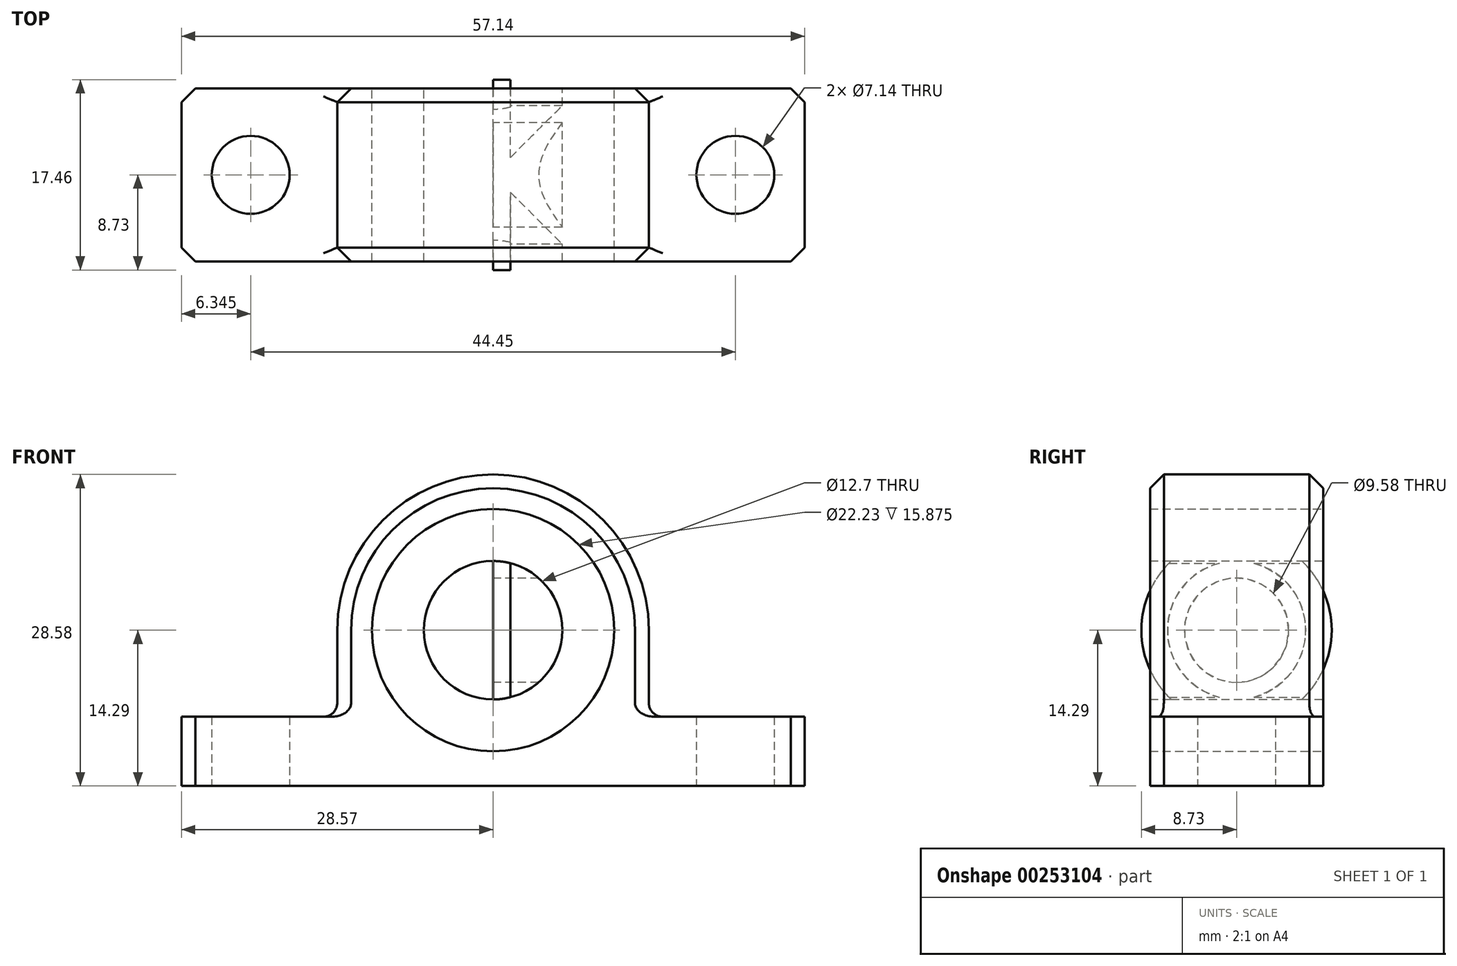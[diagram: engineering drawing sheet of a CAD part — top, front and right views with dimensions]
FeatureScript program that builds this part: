
annotation { "Feature Type Name" : "Feature", "Feature Type Description" : "" }
export const myFeature = defineFeature(function(context is Context, id is Id, definition is map)
    precondition{}
    {
        {
            var Q0;
            Q0=qCreatedBy(makeId("Front.planeOp"),FACE);
            var sketch = newSketch(context, id + "F0", { "sketchPlane" : qUnion([Q0])});
            skCircle(sketch, "E0", {"center": v(0, 0) * mm, "radius": 6.35 * mm});
            skCircle(sketch, "E1", {"center": v(0, 0) * mm, "radius": 14.29 * mm});
            skLineSegment(sketch, "E2", {"start": v(-28.58, -14.29) * mm, "end": v(28.58, -14.29) * mm});
            skLineSegment(sketch, "E3", {"start": v(0, -14.29) * mm, "end": v(0, 0) * mm, "construction": true});
            skLineSegment(sketch, "E4", {"start": v(-28.58, -14.29) * mm, "end": v(-28.58, -7.94) * mm});
            skLineSegment(sketch, "E5", {"start": v(-28.57, -7.94) * mm, "end": v(28.57, -7.94) * mm});
            skLineSegment(sketch, "E6", {"start": v(28.58, -7.94) * mm, "end": v(28.58, -14.29) * mm});
            skLineSegment(sketch, "E7", {"start": v(-14.29, -7.94) * mm, "end": v(-14.29, 0) * mm});
            skLineSegment(sketch, "E8", {"start": v(14.29, 0) * mm, "end": v(14.29, -7.94) * mm});
            skCircle(sketch, "E9", {"center": v(0, 0) * mm, "radius": 11.11 * mm});
            skSolve(sketch);
        }
        {
            var Q0;
            {var subQ1=sQuery(id+"F0.wireOp",EDGE,"E4");Q0=makeQuery(id+"F0.imprint","IMPRINT",FACE,{"disambiguationData":[TD([[makeQuery(id+"F0.imprint","IMPRINT",EDGE,{"derivedFrom":subQ1}),-1.0]])]});}
            var Q1;
            {var subQ0=sQuery(id+"F0.wireOp",EDGE,"E6");Q1=makeQuery(id+"F0.imprint","IMPRINT",FACE,{"disambiguationData":[TD([[makeQuery(id+"F0.imprint","IMPRINT",EDGE,{"derivedFrom":subQ0}),-1.0]])]});}
            var Q2;
            {var subQ1=sQuery(id+"F0.wireOp",EDGE,"E1");var subQ7=makeQuery(id+"F0.imprint","INTERSECT",VERTEX,{"derivedFrom":[subQ1,sQuery(id+"F0.wireOp",EDGE,"E2")]});Q2=makeQuery(id+"F0.imprint","IMPRINT",FACE,{"disambiguationData":[TD([[makeQuery(id+"F0.imprint","IMPRINT",EDGE,{"disambiguationData":[TD([[subQ7,1.0]])],"derivedFrom":subQ1}),1.0]])]});}
            var Q3;
            {var subQ1=sQuery(id+"F0.wireOp",EDGE,"E1");var subQ7=makeQuery(id+"F0.imprint","INTERSECT",VERTEX,{"derivedFrom":[subQ1,sQuery(id+"F0.wireOp",EDGE,"E7")]});Q3=makeQuery(id+"F0.imprint","IMPRINT",FACE,{"disambiguationData":[TD([[makeQuery(id+"F0.imprint","IMPRINT",EDGE,{"disambiguationData":[TD([[subQ7,1.0]])],"derivedFrom":subQ1}),1.0]])]});}
            var Q4;
            {var subQ0=sQuery(id+"F0.wireOp",EDGE,"E7");Q4=makeQuery(id+"F0.imprint","IMPRINT",FACE,{"disambiguationData":[TD([[makeQuery(id+"F0.imprint","IMPRINT",EDGE,{"derivedFrom":subQ0}),-1.0]])]});}
            var Q5;
            {var subQ0=sQuery(id+"F0.wireOp",EDGE,"E8");Q5=makeQuery(id+"F0.imprint","IMPRINT",FACE,{"disambiguationData":[TD([[makeQuery(id+"F0.imprint","IMPRINT",EDGE,{"derivedFrom":subQ0}),-1.0]])]});}
            extrude(context, id + "F1", {"entities" : qUnion([Q0, Q1, Q2, Q3, Q4, Q5]), "endBound" : BoundingType.SYMMETRIC, "depth" : 15.88 * mm});
        }
        {
            var Q0;
            Q0=makeQuery(id+"F0.imprint","IMPRINT",FACE,{"disambiguationData":[TD([[makeQuery(id+"F0.imprint","IMPRINT",EDGE,{"derivedFrom":sQuery(id+"F0.wireOp",EDGE,"E0")}),-1.0]])]});
            var Q1;
            {var subQ0=sQuery(id+"F0.wireOp",EDGE,"E9");var subQ1=sQuery(id+"F0.wireOp",EDGE,"E5");var subQ2=makeQuery(id+"F0.imprint","INTERSECT",VERTEX,{"disambiguationData":[OD(0.0)],"derivedFrom":[subQ1,subQ0]});Q1=makeQuery(id+"F0.imprint","IMPRINT",FACE,{"disambiguationData":[TD([[makeQuery(id+"F0.imprint","IMPRINT",EDGE,{"disambiguationData":[TD([[subQ2,-1.0]])],"derivedFrom":subQ1}),-1.0]])]});}
            extrude(context, id + "F2", {"entities" : qUnion([Q0, Q1]), "endBound" : BoundingType.SYMMETRIC, "depth" : 15.88 * mm});
        }
        {
            var Q0;
            Q0=makeQuery(id+"F1.opExtrude","CAP_EDGE",EDGE,{"disambiguationData":[OSD([sQuery(id+"F0.wireOp",EDGE,"E6")])],"isStart":true});
            var Q1;
            Q1=makeQuery(id+"F1.opExtrude","CAP_EDGE",EDGE,{"disambiguationData":[OSD([sQuery(id+"F0.wireOp",EDGE,"E4")])],"isStart":true});
            var Q2;
            Q2=makeQuery(id+"F1.opExtrude","CAP_EDGE",EDGE,{"disambiguationData":[OSD([sQuery(id+"F0.wireOp",EDGE,"E6")])],"isStart":false});
            var Q3;
            Q3=makeQuery(id+"F1.opExtrude","CAP_EDGE",EDGE,{"disambiguationData":[OSD([sQuery(id+"F0.wireOp",EDGE,"E4")])],"isStart":false});
            var Q4;
            Q4=makeQuery(id+"F1.opExtrude","CAP_EDGE",EDGE,{"disambiguationData":[OSD([sQuery(id+"F0.wireOp",EDGE,"E1")])],"isStart":false});
            var Q5;
            Q5=makeQuery(id+"F1.opExtrude","CAP_EDGE",EDGE,{"disambiguationData":[OSD([sQuery(id+"F0.wireOp",EDGE,"E1")])],"isStart":true});
            chamfer(context, id + "F3", {"entities" : qUnion([Q0, Q1, Q2, Q3, Q4, Q5]), "width" : 1.27 * mm, "tangentPropagation" : true});
        }
        {
            var Q0;
            Q0=makeQuery(id+"F1.opExtrude","SWEPT_EDGE",EDGE,{"disambiguationData":[OSD([sQuery(id+"F0.wireOp",EDGE,"E5"),sQuery(id+"F0.wireOp",EDGE,"E7")])]});
            var Q1;
            Q1=makeQuery(id+"F1.opExtrude","SWEPT_EDGE",EDGE,{"disambiguationData":[OSD([sQuery(id+"F0.wireOp",EDGE,"E5"),sQuery(id+"F0.wireOp",EDGE,"E8")])]});
            var Q2;
            {var subQ0=sQuery(id+"F0.wireOp",EDGE,"E5");var subQ1=sQuery(id+"F0.wireOp",EDGE,"E8");Q2=makeQuery(id+"F3.opChamfer","BLEND_EDGE",EDGE,{"blendedFrom":[makeQuery(id+"F1.opExtrude","CAP_EDGE",EDGE,{"disambiguationData":[OSD([subQ1])],"isStart":false}),makeQuery(id+"F1.opExtrude","SWEPT_FACE",FACE,{"disambiguationData":[OSD([subQ0]),TDD([makeQuery(id+"F0.imprint","IMPRINT",EDGE,{"disambiguationData":[TD([[makeQuery(id+"F0.imprint","INTERSECT",VERTEX,{"derivedFrom":[subQ0,sQuery(id+"F0.wireOp",EDGE,"E6")]}),1.0]])],"derivedFrom":subQ0})])]})],"blendedInto":[makeQuery(id+"F1.opExtrude","SWEPT_FACE",FACE,{"disambiguationData":[OSD([subQ0]),TDD([makeQuery(id+"F0.imprint","IMPRINT",EDGE,{"disambiguationData":[TD([[makeQuery(id+"F0.imprint","INTERSECT",VERTEX,{"derivedFrom":[subQ0,sQuery(id+"F0.wireOp",EDGE,"E6")]}),1.0]])],"derivedFrom":subQ0})])]})]});}
            var Q3;
            {var subQ0=sQuery(id+"F0.wireOp",EDGE,"E5");var subQ1=sQuery(id+"F0.wireOp",EDGE,"E8");Q3=makeQuery(id+"F3.opChamfer","BLEND_EDGE",EDGE,{"blendedFrom":[makeQuery(id+"F1.opExtrude","CAP_EDGE",EDGE,{"disambiguationData":[OSD([subQ1])],"isStart":true}),makeQuery(id+"F1.opExtrude","SWEPT_FACE",FACE,{"disambiguationData":[OSD([subQ0]),TDD([makeQuery(id+"F0.imprint","IMPRINT",EDGE,{"disambiguationData":[TD([[makeQuery(id+"F0.imprint","INTERSECT",VERTEX,{"derivedFrom":[subQ0,sQuery(id+"F0.wireOp",EDGE,"E6")]}),1.0]])],"derivedFrom":subQ0})])]})],"blendedInto":[makeQuery(id+"F1.opExtrude","SWEPT_FACE",FACE,{"disambiguationData":[OSD([subQ0]),TDD([makeQuery(id+"F0.imprint","IMPRINT",EDGE,{"disambiguationData":[TD([[makeQuery(id+"F0.imprint","INTERSECT",VERTEX,{"derivedFrom":[subQ0,sQuery(id+"F0.wireOp",EDGE,"E6")]}),1.0]])],"derivedFrom":subQ0})])]})]});}
            var Q4;
            {var subQ0=sQuery(id+"F0.wireOp",EDGE,"E5");var subQ1=sQuery(id+"F0.wireOp",EDGE,"E7");Q4=makeQuery(id+"F3.opChamfer","BLEND_EDGE",EDGE,{"blendedFrom":[makeQuery(id+"F1.opExtrude","CAP_EDGE",EDGE,{"disambiguationData":[OSD([subQ1])],"isStart":false}),makeQuery(id+"F1.opExtrude","SWEPT_FACE",FACE,{"disambiguationData":[OSD([subQ0]),TDD([makeQuery(id+"F0.imprint","IMPRINT",EDGE,{"disambiguationData":[TD([[makeQuery(id+"F0.imprint","INTERSECT",VERTEX,{"derivedFrom":[sQuery(id+"F0.wireOp",EDGE,"E4"),subQ0]}),-1.0]])],"derivedFrom":subQ0})])]})],"blendedInto":[makeQuery(id+"F1.opExtrude","SWEPT_FACE",FACE,{"disambiguationData":[OSD([subQ0]),TDD([makeQuery(id+"F0.imprint","IMPRINT",EDGE,{"disambiguationData":[TD([[makeQuery(id+"F0.imprint","INTERSECT",VERTEX,{"derivedFrom":[sQuery(id+"F0.wireOp",EDGE,"E4"),subQ0]}),-1.0]])],"derivedFrom":subQ0})])]})]});}
            var Q5;
            {var subQ0=sQuery(id+"F0.wireOp",EDGE,"E5");var subQ1=sQuery(id+"F0.wireOp",EDGE,"E7");Q5=makeQuery(id+"F3.opChamfer","BLEND_EDGE",EDGE,{"blendedFrom":[makeQuery(id+"F1.opExtrude","CAP_EDGE",EDGE,{"disambiguationData":[OSD([subQ1])],"isStart":true}),makeQuery(id+"F1.opExtrude","SWEPT_FACE",FACE,{"disambiguationData":[OSD([subQ0]),TDD([makeQuery(id+"F0.imprint","IMPRINT",EDGE,{"disambiguationData":[TD([[makeQuery(id+"F0.imprint","INTERSECT",VERTEX,{"derivedFrom":[sQuery(id+"F0.wireOp",EDGE,"E4"),subQ0]}),-1.0]])],"derivedFrom":subQ0})])]})],"blendedInto":[makeQuery(id+"F1.opExtrude","SWEPT_FACE",FACE,{"disambiguationData":[OSD([subQ0]),TDD([makeQuery(id+"F0.imprint","IMPRINT",EDGE,{"disambiguationData":[TD([[makeQuery(id+"F0.imprint","INTERSECT",VERTEX,{"derivedFrom":[sQuery(id+"F0.wireOp",EDGE,"E4"),subQ0]}),-1.0]])],"derivedFrom":subQ0})])]})]});}
            fillet(context, id + "F4", {"entities" : qUnion([Q0, Q1, Q2, Q3, Q4, Q5]), "radius" : 1.27 * mm, "allowEdgeOverflow" : false});
        }
        {
            var Q0;
            Q0=makeQuery(id+"F1.opExtrude","SWEPT_FACE",FACE,{"disambiguationData":[OSD([sQuery(id+"F0.wireOp",EDGE,"E2")])]});
            var sketch = newSketch(context, id + "F5", { "sketchPlane" : qUnion([Q0])});
            skCircle(sketch, "E10", {"center": v(-22.23, 0) * mm, "radius": 3.57 * mm});
            skPoint(sketch, "E10.centerSnap0", {"position": v(-28.58, 0) * mm});
            skLineSegment(sketch, "E11", {"start": v(0, 7.94) * mm, "end": v(0, -7.94) * mm, "construction": true});
            skCircle(sketch, "E12", {"center": v(22.23, 0) * mm, "radius": 3.57 * mm});
            skPoint(sketch, "E12.centerSnap0", {"position": v(28.58, 0) * mm});
            skSolve(sketch);
        }
        {
            var Q0;
            Q0=makeQuery(id+"F5.imprint","IMPRINT",FACE,{"disambiguationData":[TD([[makeQuery(id+"F5.imprint","IMPRINT",EDGE,{"derivedFrom":sQuery(id+"F5.wireOp",EDGE,"E10")}),1.0]])]});
            var Q1;
            Q1=makeQuery(id+"F5.imprint","IMPRINT",FACE,{"disambiguationData":[TD([[makeQuery(id+"F5.imprint","IMPRINT",EDGE,{"derivedFrom":sQuery(id+"F5.wireOp",EDGE,"E12")}),1.0]])]});
            extrude(context, id + "F6", {"entities" : qUnion([Q0, Q1]), "operationType" : NewBodyOperationType.REMOVE, "endBound" : BoundingType.THROUGH_ALL, "oppositeDirection" : true, "depth" : 25.4 * mm});
        }
        {
            var Q0;
            Q0=qCreatedBy(makeId("Right.planeOp"),FACE);
            var sketch = newSketch(context, id + "F7", { "sketchPlane" : qUnion([Q0])});
            skCircle(sketch, "E13", {"center": v(0, 0) * mm, "radius": 8.73 * mm});
            skCircle(sketch, "E14", {"center": v(0, 0) * mm, "radius": 6.35 * mm});
            skCircle(sketch, "E15", {"center": v(0, 0) * mm, "radius": 4.79 * mm});
            skSolve(sketch);
        }
        {
            var Q0;
            Q0=makeQuery(id+"F7.imprint","IMPRINT",FACE,{"disambiguationData":[TD([[makeQuery(id+"F7.imprint","IMPRINT",EDGE,{"derivedFrom":sQuery(id+"F7.wireOp",EDGE,"E14")}),1.0]])]});
            extrude(context, id + "F8", {"entities" : qUnion([Q0]), "depth" : 6.35 * mm});
        }
        {
            var Q0;
            Q0=makeQuery(id+"F7.imprint","IMPRINT",FACE,{"disambiguationData":[TD([[makeQuery(id+"F7.imprint","IMPRINT",EDGE,{"derivedFrom":sQuery(id+"F7.wireOp",EDGE,"E13")}),1.0]])]});
            var Q1;
            Q1=makeQuery(id+"F7.imprint","IMPRINT",FACE,{"disambiguationData":[TD([[makeQuery(id+"F7.imprint","IMPRINT",EDGE,{"derivedFrom":sQuery(id+"F7.wireOp",EDGE,"E14")}),1.0]])]});
            extrude(context, id + "F9", {"entities" : qUnion([Q0, Q1]), "operationType" : NewBodyOperationType.ADD, "depth" : 1.59 * mm});
        }
    });
